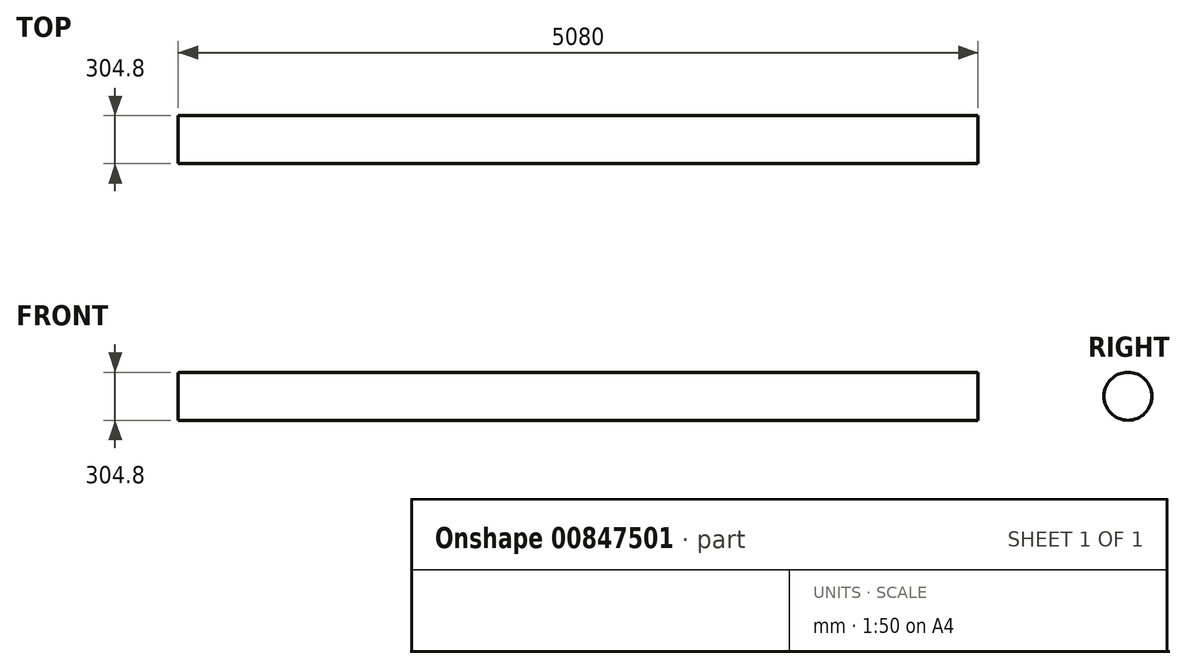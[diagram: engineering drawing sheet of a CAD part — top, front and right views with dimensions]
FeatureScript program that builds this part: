
annotation { "Feature Type Name" : "Feature", "Feature Type Description" : "" }
export const myFeature = defineFeature(function(context is Context, id is Id, definition is map)
    precondition{}
    {
        {
            var Q0;
            Q0=qCreatedBy(makeId("Right.planeOp"),FACE);
            var sketch = newSketch(context, id + "F0", { "sketchPlane" : qUnion([Q0])});
            skCircle(sketch, "E0", {"center": v(0, 0) * mm, "radius": 152.4 * mm});
            skSolve(sketch);
        }
        {
            var Q0;
            Q0=makeQuery(id+"F0.imprint","IMPRINT",FACE,{"disambiguationData":[TD([[makeQuery(id+"F0.imprint","IMPRINT",EDGE,{"derivedFrom":sQuery(id+"F0.wireOp",EDGE,"E0")}),1.0]])]});
            extrude(context, id + "F1", {"entities" : qUnion([Q0]), "depth" : 5080 * mm, "offsetDistance" : 25.4 * mm});
        }
    });
